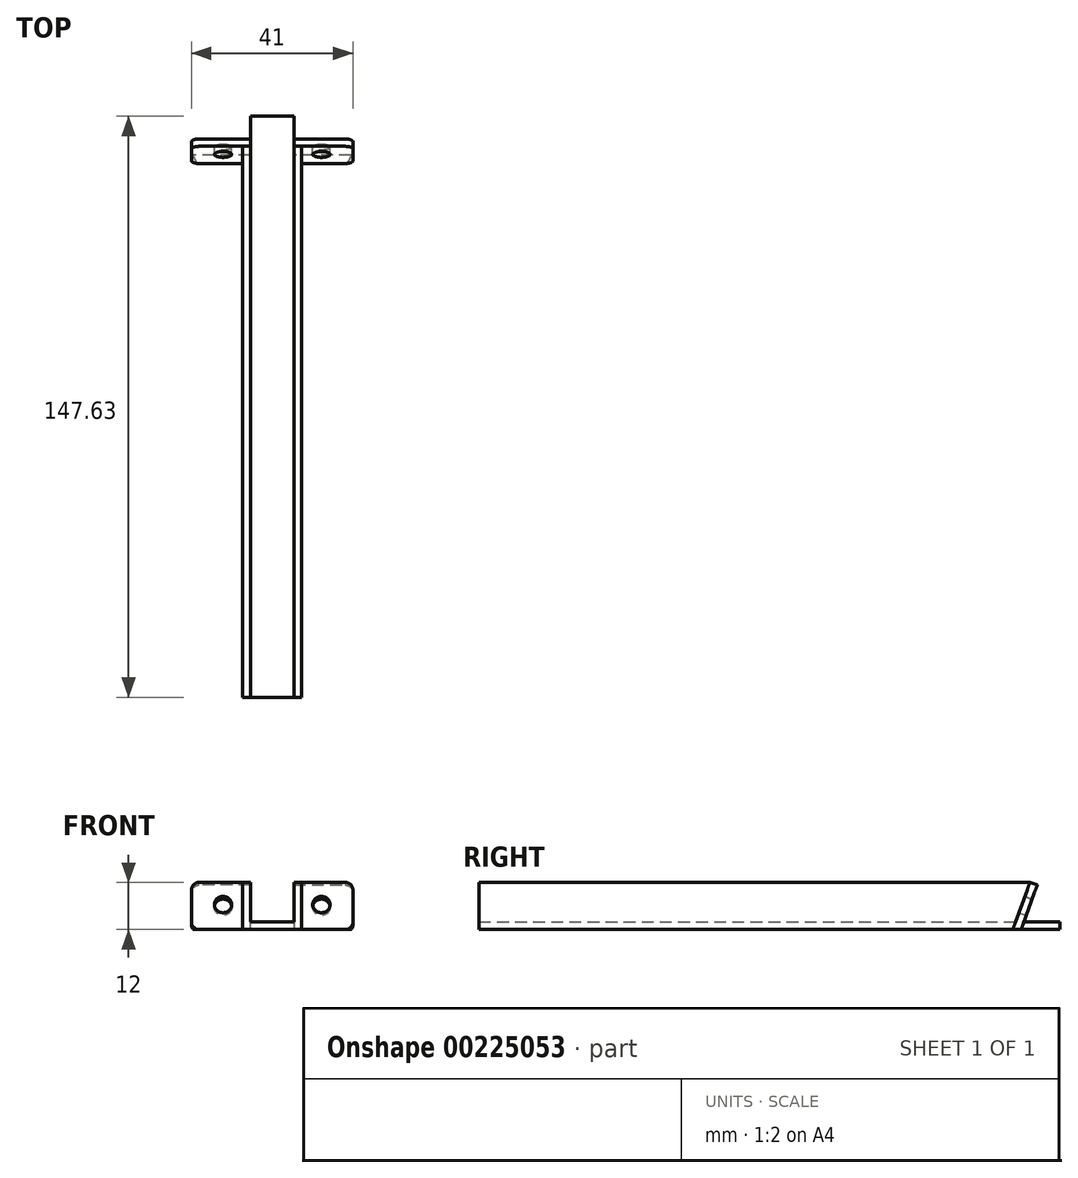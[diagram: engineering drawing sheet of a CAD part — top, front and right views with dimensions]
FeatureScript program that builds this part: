
annotation { "Feature Type Name" : "Feature", "Feature Type Description" : "" }
export const myFeature = defineFeature(function(context is Context, id is Id, definition is map)
    precondition{}
    {
        {
            var Q0;
            Q0=qCreatedBy(makeId("Front.planeOp"),FACE);
            var sketch = newSketch(context, id + "F0", { "sketchPlane" : qUnion([Q0])});
            skLineSegment(sketch, "E0.bottom", {"start": v(-7.5, 12) * mm, "end": v(-5.5, 12) * mm});
            skLineSegment(sketch, "E0.top", {"start": v(-7.5, 0) * mm, "end": v(7.5, 0) * mm});
            skLineSegment(sketch, "E0.left", {"start": v(-7.5, 12) * mm, "end": v(-7.5, 0) * mm});
            skLineSegment(sketch, "E0.right", {"start": v(7.5, 12) * mm, "end": v(7.5, 0) * mm});
            skLineSegment(sketch, "E1", {"start": v(-5.5, 12) * mm, "end": v(-5.5, 2) * mm});
            skLineSegment(sketch, "E2", {"start": v(-5.5, 2) * mm, "end": v(5.5, 2) * mm});
            skLineSegment(sketch, "E3", {"start": v(5.5, 2) * mm, "end": v(5.5, 12) * mm});
            skLineSegment(sketch, "E4.trimOffspring", {"start": v(5.5, 12) * mm, "end": v(7.5, 12) * mm});
            skSolve(sketch);
        }
        {
            var Q0;
            Q0=qSketchRegion(id+"F0",true);
            extrude(context, id + "F1", {"entities" : qUnion([Q0]), "depth" : 140 * mm});
        }
        {
            var Q0;
            Q0=makeQuery(id+"F1.opExtrude","SWEPT_FACE",FACE,{"disambiguationData":[OSD([sQuery(id+"F0.wireOp",EDGE,"E0.left")])]});
            var sketch = newSketch(context, id + "F2", { "sketchPlane" : qUnion([Q0])});
            skLineSegment(sketch, "E5", {"start": v(0, 12) * mm, "end": v(4.37, 0) * mm});
            skLineSegment(sketch, "E6", {"start": v(4.37, 0) * mm, "end": v(0, 0) * mm});
            skLineSegment(sketch, "E7", {"start": v(0, 0) * mm, "end": v(0, 12) * mm});
            skSolve(sketch);
        }
        {
            var Q0;
            Q0=qSketchRegion(id+"F2",true);
            extrude(context, id + "F3", {"entities" : qUnion([Q0]), "operationType" : NewBodyOperationType.REMOVE, "oppositeDirection" : true, "depth" : 25 * mm});
        }
        {
            var Q0;
            Q0=makeQuery(id+"F3.boolean.opBoolean","COPY",FACE,{"derivedFrom":makeQuery(id+"F3.opExtrude","SWEPT_FACE",FACE,{"disambiguationData":[OSD([sQuery(id+"F2.wireOp",EDGE,"E5")])]})});
            var sketch = newSketch(context, id + "F4", { "sketchPlane" : qUnion([Q0])});
            skLineSegment(sketch, "E8.bottom", {"start": v(-5.5, 11.28) * mm, "end": v(-20.5, 11.28) * mm});
            skLineSegment(sketch, "E8.top", {"start": v(-5.5, -1.5) * mm, "end": v(-20.5, -1.5) * mm});
            skLineSegment(sketch, "E8.left", {"start": v(-5.5, 11.28) * mm, "end": v(-5.5, -1.5) * mm});
            skLineSegment(sketch, "E8.right", {"start": v(-20.5, 11.28) * mm, "end": v(-20.5, -1.5) * mm});
            skLineSegment(sketch, "E9.bottom", {"start": v(5.5, 11.28) * mm, "end": v(20.5, 11.28) * mm});
            skLineSegment(sketch, "E9.top", {"start": v(5.5, -1.5) * mm, "end": v(20.5, -1.5) * mm});
            skLineSegment(sketch, "E9.left", {"start": v(5.5, 11.28) * mm, "end": v(5.5, -1.5) * mm});
            skLineSegment(sketch, "E9.right", {"start": v(20.5, 11.28) * mm, "end": v(20.5, -1.5) * mm});
            skSolve(sketch);
        }
        {
            var Q0;
            Q0 = qSketchRegion(id + "F4", true);
            extrude(context, id + "F5", {"entities" : qUnion([Q0]), "operationType" : NewBodyOperationType.ADD, "depth" : 2 * mm});
        }
        {
            var Q0;
            Q0=makeQuery(id+"F5.opExtrude","SWEPT_EDGE",EDGE,{"disambiguationData":[OSD([sQuery(id+"F4.wireOp",EDGE,"E8.bottom"),sQuery(id+"F4.wireOp",EDGE,"E8.right")])]});
            var Q1;
            Q1=makeQuery(id+"F5.opExtrude","SWEPT_EDGE",EDGE,{"disambiguationData":[OSD([sQuery(id+"F4.wireOp",EDGE,"E9.bottom"),sQuery(id+"F4.wireOp",EDGE,"E9.right")])]});
            var Q2;
            Q2=makeQuery(id+"FAph9uxltRurJvv_1.opExtrude","CAP_EDGE",EDGE,{"disambiguationData":[OSD([sQuery(id+"Fnsm4xSgVClunSC_1.wireOp",EDGE,"w1TH2Y56-oDBd-SurU-cjZt-78lEezf8W6AD.right")])],"isStart":false});
            var Q3;
            Q3=makeQuery(id+"FAph9uxltRurJvv_1.opExtrude","CAP_EDGE",EDGE,{"disambiguationData":[OSD([sQuery(id+"Fnsm4xSgVClunSC_1.wireOp",EDGE,"w1TH2Y56-oDBd-SurU-cjZt-78lEezf8W6AD.left")])],"isStart":false});
            var Q4;
            Q4=makeQuery(id+"F5.opExtrude","SWEPT_EDGE",EDGE,{"disambiguationData":[OSD([sQuery(id+"F4.wireOp",EDGE,"E8.top"),sQuery(id+"F4.wireOp",EDGE,"E8.right")])]});
            var Q5;
            Q5=makeQuery(id+"F5.opExtrude","SWEPT_EDGE",EDGE,{"disambiguationData":[OSD([sQuery(id+"F4.wireOp",EDGE,"E9.top"),sQuery(id+"F4.wireOp",EDGE,"E9.right")])]});
            fillet(context, id + "F6", {"entities" : qUnion([Q0, Q1, Q2, Q3, Q4, Q5]), "radius" : 2 * mm, "tangentPropagation" : true, "allowEdgeOverflow" : false});
        }
        {
            var Q0;
            Q0=makeQuery(id+"F1.opExtrude","SWEPT_FACE",FACE,{"disambiguationData":[OSD([sQuery(id+"F0.wireOp",EDGE,"E0.top")])]});
            var sketch = newSketch(context, id + "F7", { "sketchPlane" : qUnion([Q0])});
            skLineSegment(sketch, "E10.bottom", {"start": v(-5.5, 4.37) * mm, "end": v(5.5, 4.37) * mm});
            skLineSegment(sketch, "E10.top", {"start": v(-5.5, -7.63) * mm, "end": v(5.5, -7.63) * mm});
            skLineSegment(sketch, "E10.left", {"start": v(-5.5, 4.37) * mm, "end": v(-5.5, -7.63) * mm});
            skLineSegment(sketch, "E10.right", {"start": v(5.5, 4.37) * mm, "end": v(5.5, -7.63) * mm});
            skSolve(sketch);
        }
        {
            var Q0;
            Q0=makeQuery(id+"F7.imprint","IMPRINT",FACE,{"disambiguationData":[TD([[makeQuery(id+"F7.imprint","IMPRINT",EDGE,{"derivedFrom":sQuery(id+"F7.wireOp",EDGE,"E10.bottom")}),1.0]])]});
            extrude(context, id + "F8", {"entities" : qUnion([Q0]), "operationType" : NewBodyOperationType.ADD, "oppositeDirection" : true, "depth" : 2 * mm});
        }
        {
            var Q0;
            Q0=makeQuery(id+"F8.opExtrude","SWEPT_FACE",FACE,{"disambiguationData":[OSD([sQuery(id+"F7.wireOp",EDGE,"E10.left")])]});
            var sketch = newSketch(context, id + "F9", { "sketchPlane" : qUnion([Q0])});
            skLineSegment(sketch, "E11.bottom", {"start": v(-7.63, 0) * mm, "end": v(7.07, 0) * mm});
            skLineSegment(sketch, "E11.top", {"start": v(-7.63, -1.85) * mm, "end": v(7.07, -1.85) * mm});
            skLineSegment(sketch, "E11.left", {"start": v(-7.63, 0) * mm, "end": v(-7.63, -1.85) * mm});
            skLineSegment(sketch, "E11.right", {"start": v(7.07, 0) * mm, "end": v(7.07, -1.85) * mm});
            skSolve(sketch);
        }
        {
            var Q0;
            Q0=makeQuery(id+"F9.imprint","IMPRINT",FACE,{"disambiguationData":[TD([[makeQuery(id+"F9.imprint","IMPRINT",EDGE,{"derivedFrom":sQuery(id+"F9.wireOp",EDGE,"E11.top")}),1.0]])]});
            extrude(context, id + "F10", {"entities" : qUnion([Q0]), "operationType" : NewBodyOperationType.REMOVE, "endBound" : BoundingType.SYMMETRIC, "depth" : 100 * mm});
        }
        {
            var Q0;
            Q0=makeQuery(id+"F5.opExtrude","CAP_FACE",FACE,{"disambiguationData":[OSD([sQuery(id+"F4.wireOp",EDGE,"E8.bottom"),sQuery(id+"F4.wireOp",EDGE,"E8.top"),sQuery(id+"F4.wireOp",EDGE,"E8.left"),sQuery(id+"F4.wireOp",EDGE,"E8.right")])],"isStart":false});
            var sketch = newSketch(context, id + "F11", { "sketchPlane" : qUnion([Q0])});
            skPoint(sketch, "E12", {"position": v(-12.5, 5.28) * mm});
            skPoint(sketch, "E13", {"position": v(12.5, 5.28) * mm});
            skSolve(sketch);
        }
        {
            var Q0;
            Q0=sQuery(id+"F11.wireOp",VERTEX,"E12");
            var Q1;
            Q1=sQuery(id+"F11.wireOp",VERTEX,"E13");
            var Q2;
            Q2=makeQuery(id+"F1.opExtrude","SWEPT_BODY",BODY,{"disambiguationData":[OSD([sQuery(id+"F0.wireOp",EDGE,"E0.bottom"),sQuery(id+"F0.wireOp",EDGE,"E0.top"),sQuery(id+"F0.wireOp",EDGE,"E0.left"),sQuery(id+"F0.wireOp",EDGE,"E0.right"),sQuery(id+"F0.wireOp",EDGE,"E1"),sQuery(id+"F0.wireOp",EDGE,"E2"),sQuery(id+"F0.wireOp",EDGE,"E3"),sQuery(id+"F0.wireOp",EDGE,"E4.trimOffspring")])]});
            hole(context, id + "F12", {"style" : HoleStyle.SIMPLE, "endStyle" : HoleEndStyle.THROUGH, "standardTappedOrClearance" : lookupTablePath({ "standard" : "ISO", "fit" : "Normal", "size" : "M4", "type" : "Clearance" }), "standardBlindInLast" : lookupTablePath({ "fit" : "Standard", "standard" : "ISO", "size" : "M4", "type" : "Clearance" }), "holeDiameter" : 4.4 * mm, "tappedDepth" : 12 * mm, "tapClearance" : 3, "locations" : qUnion([Q0, Q1]), "scope" : qUnion([Q2])});
        }
    });
